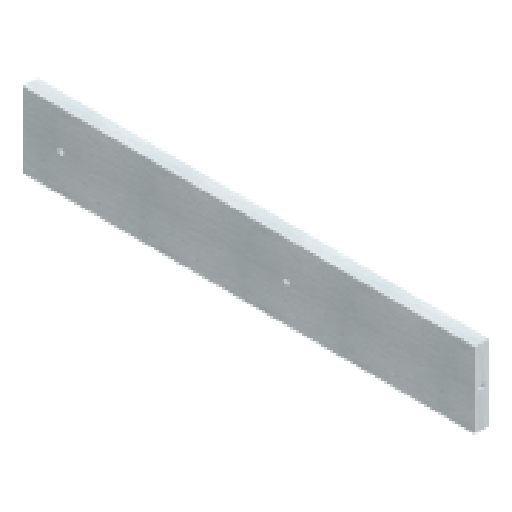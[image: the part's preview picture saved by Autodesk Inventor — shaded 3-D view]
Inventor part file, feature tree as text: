
AUTODESK INVENTOR PART (.ipt)
format: ipt  version: 2024 (Build 280153000, 153)  size: 116,736 bytes
history: native  units: in
note: dims shown in document units (in); Inventor stores cm internally (conversion verified against a paired STEP export)
features: sketch x5, extrude x4
ambient origin geometry x8: Origin, YZ Plane, XZ Plane, XY Plane, X Axis, Y Axis, Z Axis, Center Point
bodies: Solid1 (feature_tree)
feature tree (9):
  sketch  "Sketch1"  dims[d0=23.622in d1=3.937in]
  extrude  "Extrusion1"  Depth=3.937in
  extrude  "Extrusion2"  Depth=0.374in
  extrude  "Extrusion3"  Depth=0.315in
  extrude  "Extrusion4"  Depth=0.4331in TaperAngle=0.0deg
  sketch  "Sketch2"  dims[d2=0.374in d3=0.374in d4=0.0in d5=0.0in d6=1.9685in]
  sketch  "Sketch3"  dims[d7=9.8425in d8=0.315in]
  sketch  "Sketch4"  dims[d9=0.315in d10=0.4331in d11=0.0in]
  sketch  "Sketch5"  dims[d12=0.315in d13=0.4331in d14=0.0in d15=0.315in d16=0.4331in d17=0.0in]
